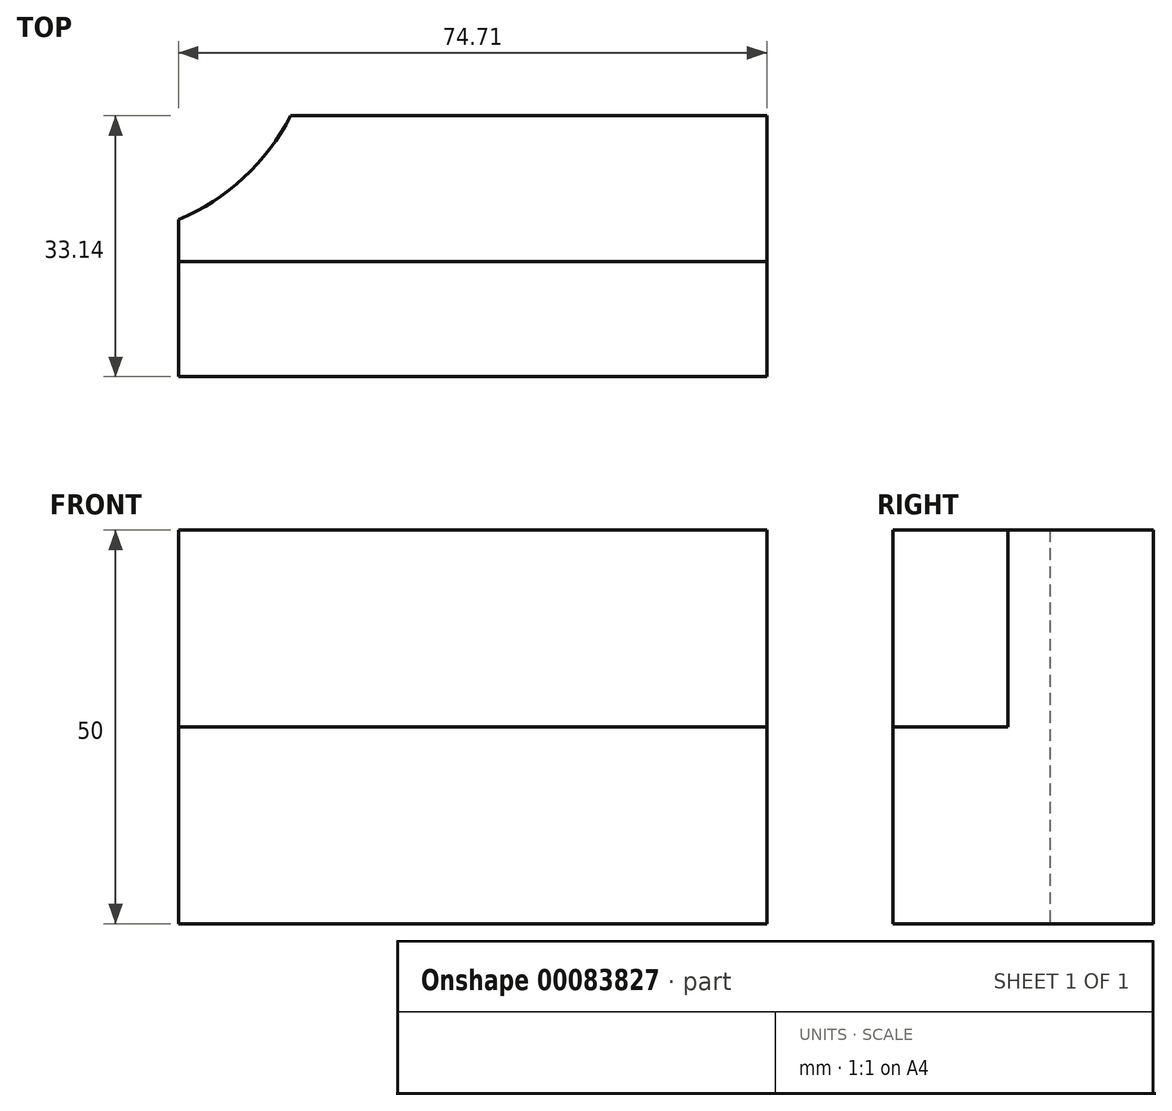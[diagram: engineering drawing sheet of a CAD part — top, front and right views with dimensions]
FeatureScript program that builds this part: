
annotation { "Feature Type Name" : "Feature", "Feature Type Description" : "" }
export const myFeature = defineFeature(function(context is Context, id is Id, definition is map)
    precondition{}
    {
        {
            var Q0;
            Q0=qCreatedBy(makeId("Top.planeOp"),FACE);
            var sketch = newSketch(context, id + "F0", { "sketchPlane" : qUnion([Q0])});
            skLineSegment(sketch, "E0.bottom", {"start": v(0, 0) * mm, "end": v(-74.71, 0) * mm});
            skLineSegment(sketch, "E0.top", {"start": v(0, 14.6) * mm, "end": v(-74.71, 14.6) * mm});
            skLineSegment(sketch, "E0.left", {"start": v(0, 0) * mm, "end": v(0, 14.6) * mm});
            skLineSegment(sketch, "E0.right", {"start": v(-74.71, 0) * mm, "end": v(-74.71, 14.6) * mm});
            skLineSegment(sketch, "E1.top", {"start": v(0, 33.14) * mm, "end": v(-74.71, 33.14) * mm});
            skLineSegment(sketch, "E1.left", {"start": v(0, 14.6) * mm, "end": v(0, 33.14) * mm});
            skLineSegment(sketch, "E1.right", {"start": v(-74.71, 14.6) * mm, "end": v(-74.71, 33.14) * mm});
            skCircle(sketch, "E2", {"center": v(-51.22, 50.74) * mm, "radius": 7.45 * mm});
            skCircle(sketch, "E3", {"center": v(-47.05, -24.17) * mm, "radius": 17.34 * mm});
            skCircle(sketch, "E4", {"center": v(-85.46, 45.81) * mm, "radius": 28 * mm});
            skSolve(sketch);
        }
        {
            var Q0;
            Q0=makeQuery(id+"F0.imprint","IMPRINT",FACE,{"disambiguationData":[TD([[makeQuery(id+"F0.imprint","IMPRINT",EDGE,{"derivedFrom":sQuery(id+"F0.wireOp",EDGE,"E0.top")}),-1.0]])]});
            var Q1;
            Q1=makeQuery(id+"F0.imprint","IMPRINT",FACE,{"disambiguationData":[TD([[makeQuery(id+"F0.imprint","IMPRINT",EDGE,{"derivedFrom":sQuery(id+"F0.wireOp",EDGE,"E0.bottom")}),-1.0]])]});
            extrude(context, id + "F1", {"entities" : qUnion([Q0, Q1]), "depth" : 25 * mm, "hasSecondDirection" : true, "secondDirectionOppositeDirection" : true, "secondDirectionDepth" : 25 * mm});
        }
        {
            var Q0;
            Q0=makeQuery(id+"F0.imprint","IMPRINT",FACE,{"disambiguationData":[TD([[makeQuery(id+"F0.imprint","IMPRINT",EDGE,{"derivedFrom":sQuery(id+"F0.wireOp",EDGE,"E0.bottom")}),-1.0]])]});
            extrude(context, id + "F2", {"entities" : qUnion([Q0]), "depth" : 25 * mm});
        }
    });
